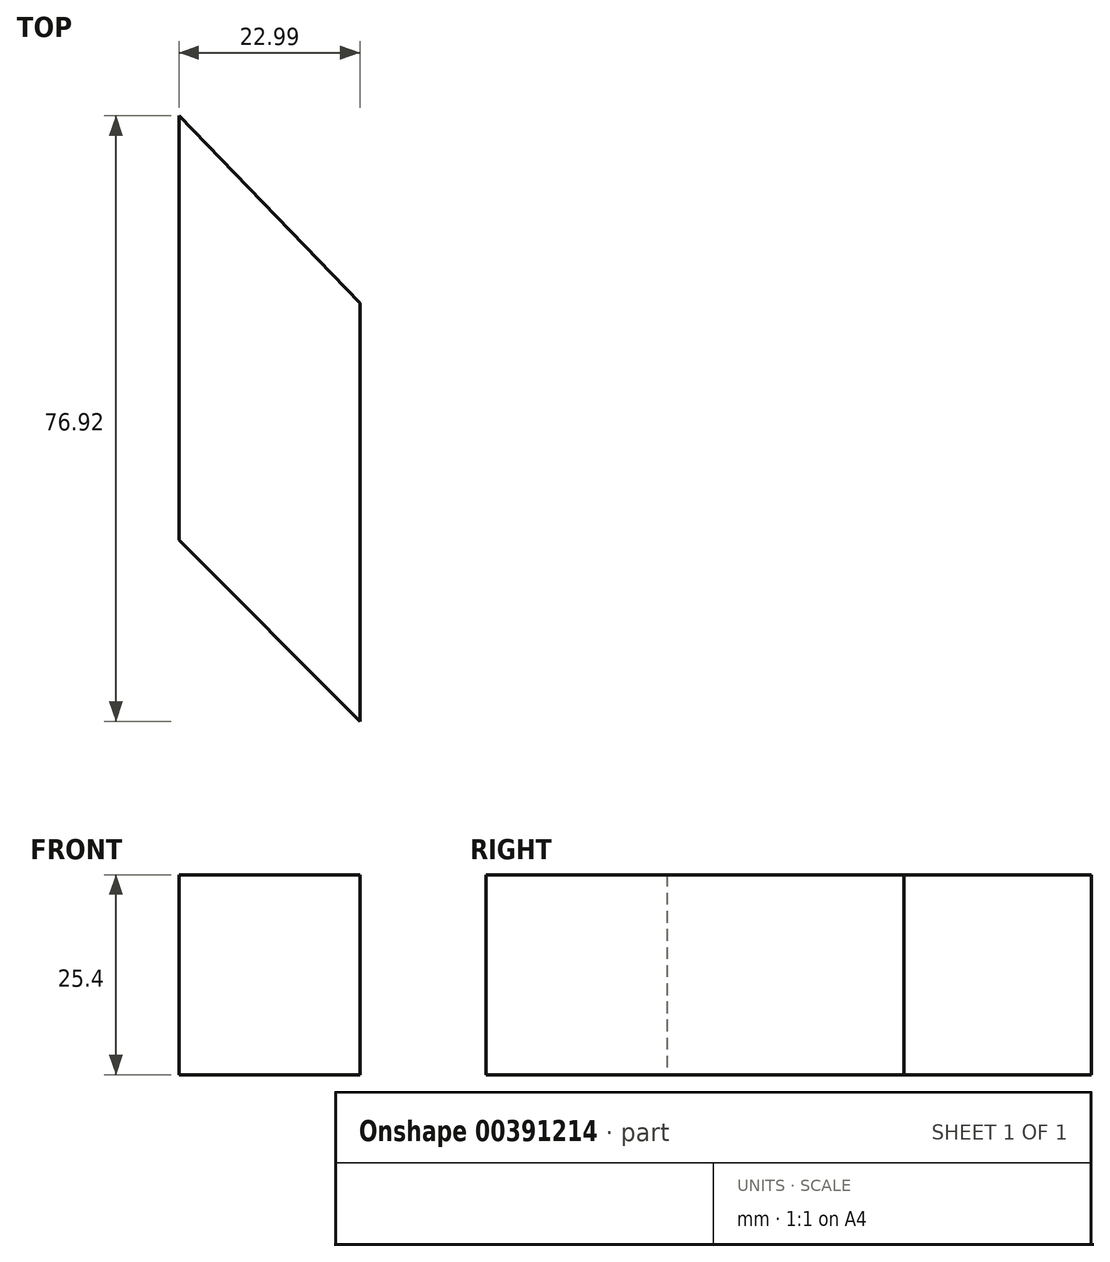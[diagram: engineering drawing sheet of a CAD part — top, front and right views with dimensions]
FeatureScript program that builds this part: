
annotation { "Feature Type Name" : "Feature", "Feature Type Description" : "" }
export const myFeature = defineFeature(function(context is Context, id is Id, definition is map)
    precondition{}
    {
        {
            var Q0;
            Q0=qCreatedBy(makeId("Top.planeOp"),FACE);
            var sketch = newSketch(context, id + "F0", { "sketchPlane" : qUnion([Q0])});
            skLineSegment(sketch, "E0", {"start": v(-86.57, -55.16) * mm, "end": v(-86.57, -74.48) * mm});
            skLineSegment(sketch, "E1", {"start": v(-86.57, -74.48) * mm, "end": v(-235, 74.06) * mm});
            skLineSegment(sketch, "E2", {"start": v(-235, 74.06) * mm, "end": v(-235, 127.98) * mm});
            skLineSegment(sketch, "E3", {"start": v(-235, 127.98) * mm, "end": v(-212.02, 104.17) * mm});
            skLineSegment(sketch, "E4", {"start": v(-212.02, 104.17) * mm, "end": v(-212.02, 51.06) * mm});
            skSolve(sketch);
        }
        {
            var Q0;
            {var subQ0=sQuery(id+"F0.wireOp",EDGE,"E2");Q0=makeQuery(id+"F0.imprint","IMPRINT",FACE,{"disambiguationData":[TD([[makeQuery(id+"F0.imprint","IMPRINT",EDGE,{"derivedFrom":subQ0}),-1.0]])]});}
            extrude(context, id + "F1", {"entities" : qUnion([Q0]), "depth" : 25.4 * mm});
        }
    });
